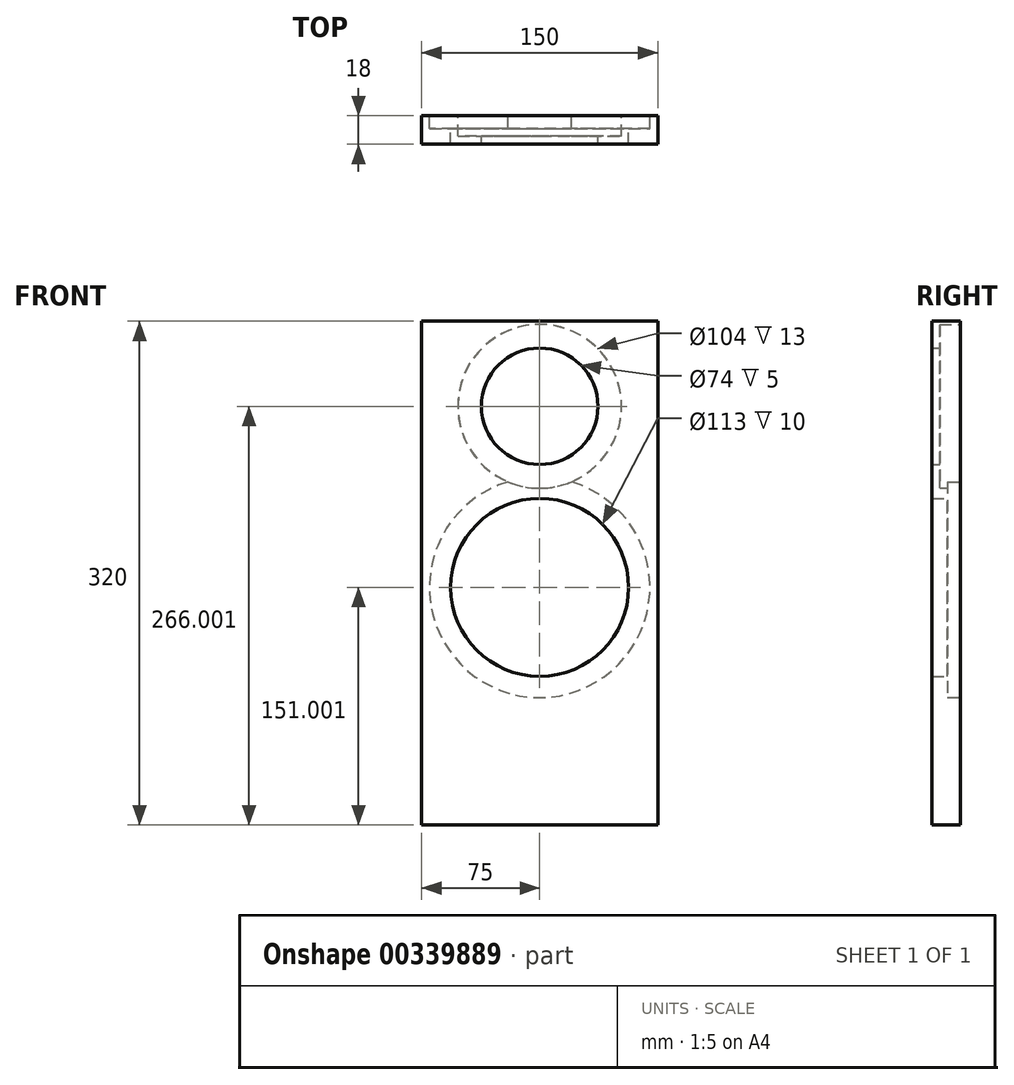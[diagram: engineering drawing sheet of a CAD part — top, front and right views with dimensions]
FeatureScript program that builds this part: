
annotation { "Feature Type Name" : "Feature", "Feature Type Description" : "" }
export const myFeature = defineFeature(function(context is Context, id is Id, definition is map)
    precondition{}
    {
        {
            var Q0;
            Q0=qCreatedBy(makeId("Front.planeOp"),FACE);
            var sketch = newSketch(context, id + "F0", { "sketchPlane" : qUnion([Q0])});
            skLineSegment(sketch, "E0.bottom", {"start": v(-23.75, 201.73) * mm, "end": v(126.25, 201.73) * mm});
            skLineSegment(sketch, "E0.top", {"start": v(-23.75, -118.27) * mm, "end": v(126.25, -118.27) * mm});
            skLineSegment(sketch, "E0.left", {"start": v(-23.75, 201.73) * mm, "end": v(-23.75, -118.27) * mm});
            skLineSegment(sketch, "E0.right", {"start": v(126.25, 201.73) * mm, "end": v(126.25, -118.27) * mm});
            skLineSegment(sketch, "E1", {"start": v(51.25, 201.73) * mm, "end": v(51.25, -118.27) * mm, "construction": true});
            skCircle(sketch, "E2", {"center": v(51.25, 147.73) * mm, "radius": 52 * mm});
            skCircle(sketch, "E3", {"center": v(51.25, 147.73) * mm, "radius": 37 * mm});
            skCircle(sketch, "E4", {"center": v(51.25, 147.73) * mm, "radius": 42.5 * mm, "construction": true});
            skCircle(sketch, "E5", {"center": v(51.25, 32.73) * mm, "radius": 70 * mm});
            skCircle(sketch, "E6", {"center": v(51.25, 32.73) * mm, "radius": 56.5 * mm});
            skSolve(sketch);
        }
        {
            var Q0;
            Q0 = qSketchRegion(id + "F0", true);
            var Q1;
            Q1=makeQuery(id+"F0.imprint","IMPRINT",FACE,{"disambiguationData":[TD([[makeQuery(id+"F0.imprint","IMPRINT",EDGE,{"derivedFrom":sQuery(id+"F0.wireOp",EDGE,"E6")}),1.0]])]});
            var Q2;
            Q2=makeQuery(id+"F0.imprint","IMPRINT",FACE,{"disambiguationData":[TD([[makeQuery(id+"F0.imprint","IMPRINT",EDGE,{"derivedFrom":sQuery(id+"F0.wireOp",EDGE,"E6")}),-1.0]])]});
            var Q3;
            Q3=makeQuery(id+"F0.imprint","IMPRINT",FACE,{"disambiguationData":[TD([[makeQuery(id+"F0.imprint","IMPRINT",EDGE,{"derivedFrom":sQuery(id+"F0.wireOp",EDGE,"E3")}),1.0]])]});
            var Q4;
            Q4=makeQuery(id+"F0.imprint","IMPRINT",FACE,{"disambiguationData":[TD([[makeQuery(id+"F0.imprint","IMPRINT",EDGE,{"derivedFrom":sQuery(id+"F0.wireOp",EDGE,"E3")}),-1.0]])]});
            var Q5;
            {var subQ0=sQuery(id+"F0.wireOp",EDGE,"E5");var subQ1=sQuery(id+"F0.wireOp",EDGE,"E2");var subQ2=makeQuery(id+"F0.imprint","INTERSECT",VERTEX,{"disambiguationData":[OD(0.0)],"derivedFrom":[subQ1,subQ0]});Q5=makeQuery(id+"F0.imprint","IMPRINT",FACE,{"disambiguationData":[TD([[makeQuery(id+"F0.imprint","IMPRINT",EDGE,{"disambiguationData":[TD([[subQ2,-1.0]])],"derivedFrom":subQ1}),1.0]])]});}
            extrude(context, id + "F1", {"entities" : qUnion([Q0, Q1, Q2, Q3, Q4, Q5]), "depth" : 18 * mm, "offsetDistance" : 25 * mm});
        }
        {
            var Q0;
            Q0=makeQuery(id+"F0.imprint","IMPRINT",FACE,{"disambiguationData":[TD([[makeQuery(id+"F0.imprint","IMPRINT",EDGE,{"derivedFrom":sQuery(id+"F0.wireOp",EDGE,"E6")}),1.0]])]});
            var Q1;
            Q1=makeQuery(id+"F0.imprint","IMPRINT",FACE,{"disambiguationData":[TD([[makeQuery(id+"F0.imprint","IMPRINT",EDGE,{"derivedFrom":sQuery(id+"F0.wireOp",EDGE,"E6")}),-1.0]])]});
            var Q2;
            {var subQ0=sQuery(id+"F0.wireOp",EDGE,"E5");var subQ1=sQuery(id+"F0.wireOp",EDGE,"E2");var subQ2=makeQuery(id+"F0.imprint","INTERSECT",VERTEX,{"disambiguationData":[OD(0.0)],"derivedFrom":[subQ1,subQ0]});Q2=makeQuery(id+"F0.imprint","IMPRINT",FACE,{"disambiguationData":[TD([[makeQuery(id+"F0.imprint","IMPRINT",EDGE,{"disambiguationData":[TD([[subQ2,-1.0]])],"derivedFrom":subQ1}),1.0]])]});}
            extrude(context, id + "F2", {"entities" : qUnion([Q0, Q1, Q2]), "operationType" : NewBodyOperationType.REMOVE, "depth" : 8 * mm, "offsetDistance" : 25 * mm});
        }
        {
            var Q0;
            Q0=makeQuery(id+"F0.imprint","IMPRINT",FACE,{"disambiguationData":[TD([[makeQuery(id+"F0.imprint","IMPRINT",EDGE,{"derivedFrom":sQuery(id+"F0.wireOp",EDGE,"E3")}),1.0]])]});
            var Q1;
            Q1=makeQuery(id+"F0.imprint","IMPRINT",FACE,{"disambiguationData":[TD([[makeQuery(id+"F0.imprint","IMPRINT",EDGE,{"derivedFrom":sQuery(id+"F0.wireOp",EDGE,"E3")}),-1.0]])]});
            var Q2;
            {var subQ0=sQuery(id+"F0.wireOp",EDGE,"E5");var subQ1=sQuery(id+"F0.wireOp",EDGE,"E2");var subQ2=makeQuery(id+"F0.imprint","INTERSECT",VERTEX,{"disambiguationData":[OD(0.0)],"derivedFrom":[subQ1,subQ0]});Q2=makeQuery(id+"F0.imprint","IMPRINT",FACE,{"disambiguationData":[TD([[makeQuery(id+"F0.imprint","IMPRINT",EDGE,{"disambiguationData":[TD([[subQ2,-1.0]])],"derivedFrom":subQ1}),1.0]])]});}
            extrude(context, id + "F3", {"entities" : qUnion([Q0, Q1, Q2]), "operationType" : NewBodyOperationType.REMOVE, "depth" : 13 * mm, "offsetDistance" : 25 * mm});
        }
        {
            var Q0;
            Q0=makeQuery(id+"F0.imprint","IMPRINT",FACE,{"disambiguationData":[TD([[makeQuery(id+"F0.imprint","IMPRINT",EDGE,{"derivedFrom":sQuery(id+"F0.wireOp",EDGE,"E3")}),1.0]])]});
            extrude(context, id + "F4", {"entities" : qUnion([Q0]), "operationType" : NewBodyOperationType.REMOVE, "depth" : 25 * mm, "offsetDistance" : 25 * mm});
        }
        {
            var Q0;
            Q0=makeQuery(id+"F0.imprint","IMPRINT",FACE,{"disambiguationData":[TD([[makeQuery(id+"F0.imprint","IMPRINT",EDGE,{"derivedFrom":sQuery(id+"F0.wireOp",EDGE,"E6")}),1.0]])]});
            extrude(context, id + "F5", {"entities" : qUnion([Q0]), "operationType" : NewBodyOperationType.REMOVE, "depth" : 25 * mm, "offsetDistance" : 25 * mm});
        }
    });
